# Revit family: STS-10260_RV17_LOD400 — копия
name_source: partatom
category: Электрооборудование
revit_build: Autodesk Revit 2017 (Build: 20170118_1100(x64)
units: mm (PartAtom-declared; Revit-internal decimal feet)

## family parameters
Всегда вертикально = Нет
Конфигурация панели = Два столбца, слева направо
На основе рабочей плоскости = Да
Общий = Нет
При загрузке вырезать с полостями = Нет
Размер круглого соединителя = Использовать диаметр
Тип детали = Щит
Точка расчета площади = Нет

## types (1)
- STS-10260
    ADSK_URL страницы изделия = https://stilsoft.ru
    ADSK_Единица измерения = шт.
    ADSK_Завод-изготовитель = ООО «Основа Безопасности»
    ADSK_Количество = 1
    ADSK_Марка = СТВФ.426479.101
    ADSK_Масса = 2.3
    ADSK_Наименование = Прожектор видимого диапазона STS-10260
    ADSK_Размер_Высота = 73 мм
    ADSK_Размер_Длина = 230 мм
    ADSK_Размер_Ширина = 145 мм
    d_короба = 20 мм
    Вариант исполнения = уличный
    Время восстановления работоспособности в условиях эксплуатации, не более, мин = 30
    Гальванически развязанный интерфейс управления = RS-485
    Дальность излучения при мощности 100%, не менее, м = 200 мм
    Индекс цветопередачи, Ra = 64
    Коэффициент мощности, не более, Вт = 0.998
    Максимальная и осевая сила света при мощьности 100%, Кд = 50000
    Максимальная и осевая сила света при мощьности 50%, Кд = 28500
    Мощность = 45
    Напряжение = 30
    Напряжение электропитания постоянного тока, В = от 10,5 до 30
    Отметка по умолчанию = 1219 мм
    Потребляемая мощность при 100%, не более, Вт = 45
    Потребляемая мощность при 50%, не более, Вт = 25
    Световой поток, Люмен при мощьности 100% = 3000
    Световой поток, Люмен при мощьности 50% = 1900
    Среднее время наработки на отказ, не менее, ч = 30000
    Угол излучения, град = 15.00°
    Цветовая температура, К = 5600
